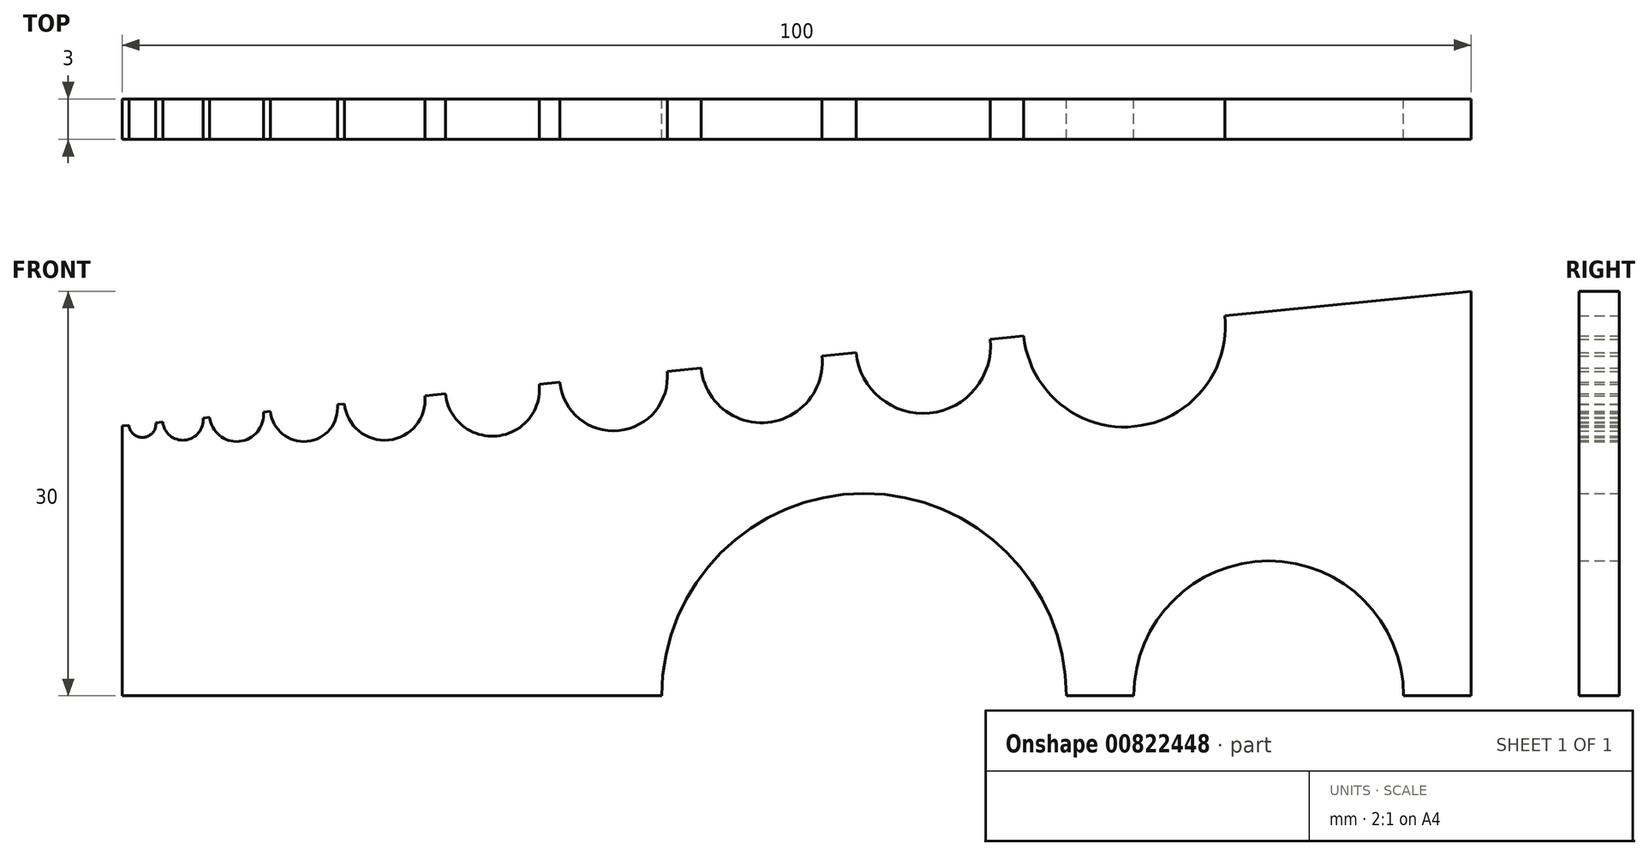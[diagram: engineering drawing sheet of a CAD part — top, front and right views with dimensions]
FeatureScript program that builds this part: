
annotation { "Feature Type Name" : "Feature", "Feature Type Description" : "" }
export const myFeature = defineFeature(function(context is Context, id is Id, definition is map)
    precondition{}
    {
        {
            var Q0;
            Q0=qCreatedBy(makeId("Front.planeOp"),FACE);
            var sketch = newSketch(context, id + "F0", { "sketchPlane" : qUnion([Q0])});
            skLineSegment(sketch, "E0", {"start": v(0, 0) * mm, "end": v(0, 20) * mm});
            skLineSegment(sketch, "E1", {"start": v(0, 20) * mm, "end": v(0.5, 20.05) * mm});
            skLineSegment(sketch, "E2", {"start": v(100, 30) * mm, "end": v(100, 0) * mm});
            skLineSegment(sketch, "E3", {"start": v(100, 0) * mm, "end": v(95, 0) * mm});
            skArc(sketch, "E4", {"start": v(0.5, 20.05) * mm, "mid": v(1.6, 19.15) * mm, "end": v(2.49, 20.25) * mm});
            skLineSegment(sketch, "E5.trimOffspring", {"start": v(2.49, 20.25) * mm, "end": v(3, 20.3) * mm});
            skArc(sketch, "E6", {"start": v(3, 20.3) * mm, "mid": v(4.64, 18.96) * mm, "end": v(5.99, 20.6) * mm});
            skLineSegment(sketch, "E7.trimOffspring", {"start": v(5.99, 20.6) * mm, "end": v(6.48, 20.65) * mm});
            skArc(sketch, "E8", {"start": v(6.48, 20.65) * mm, "mid": v(8.67, 18.86) * mm, "end": v(10.46, 21.05) * mm});
            skLineSegment(sketch, "E9.trimOffspring", {"start": v(10.46, 21.05) * mm, "end": v(10.98, 21.1) * mm});
            skArc(sketch, "E10", {"start": v(10.98, 21.1) * mm, "mid": v(13.71, 18.86) * mm, "end": v(15.95, 21.6) * mm});
            skLineSegment(sketch, "E11.trimOffspring", {"start": v(15.95, 21.6) * mm, "end": v(16.47, 21.65) * mm});
            skArc(sketch, "E12", {"start": v(16.47, 21.65) * mm, "mid": v(19.75, 18.96) * mm, "end": v(22.44, 22.24) * mm});
            skLineSegment(sketch, "E13.trimOffspring", {"start": v(22.44, 22.24) * mm, "end": v(23.95, 22.4) * mm});
            skArc(sketch, "E14", {"start": v(23.95, 22.4) * mm, "mid": v(27.78, 19.26) * mm, "end": v(30.92, 23.1) * mm});
            skArc(sketch, "E15", {"start": v(32.44, 23.24) * mm, "mid": v(36.82, 19.66) * mm, "end": v(40.4, 24.04) * mm});
            skArc(sketch, "E16", {"start": v(42.92, 24.3) * mm, "mid": v(47.85, 20.26) * mm, "end": v(51.88, 25.19) * mm});
            skArc(sketch, "E17", {"start": v(54.4, 25.44) * mm, "mid": v(59.87, 20.96) * mm, "end": v(64.35, 26.44) * mm});
            skLineSegment(sketch, "E18.trimOffspring", {"start": v(30.92, 23.1) * mm, "end": v(32.44, 23.24) * mm});
            skLineSegment(sketch, "E19.trimOffspring", {"start": v(40.4, 24.04) * mm, "end": v(42.92, 24.3) * mm});
            skLineSegment(sketch, "E20.trimOffspring", {"start": v(51.88, 25.19) * mm, "end": v(54.4, 25.44) * mm});
            skLineSegment(sketch, "E21.trimOffspring", {"start": v(64.35, 26.44) * mm, "end": v(66.84, 26.68) * mm});
            skArc(sketch, "E22", {"start": v(66.84, 26.68) * mm, "mid": v(75.05, 19.97) * mm, "end": v(81.76, 28.18) * mm});
            skLineSegment(sketch, "E23.trimOffspring", {"start": v(81.76, 28.18) * mm, "end": v(100, 30) * mm});
            skArc(sketch, "E24", {"start": v(95, 0) * mm, "mid": v(85, 10) * mm, "end": v(75, 0) * mm});
            skLineSegment(sketch, "E25.trimOffspring", {"start": v(75, 0) * mm, "end": v(70, 0) * mm});
            skArc(sketch, "E26", {"start": v(70, 0) * mm, "mid": v(55, 15) * mm, "end": v(40, 0) * mm});
            skLineSegment(sketch, "E27.trimOffspring", {"start": v(40, 0) * mm, "end": v(0, 0) * mm});
            skSolve(sketch);
        }
        {
            var Q0;
            Q0 = qSketchRegion(id + "F0", true);
            extrude(context, id + "F1", {"entities" : qUnion([Q0]), "depth" : 3 * mm, "offsetDistance" : 25 * mm});
        }
    });
